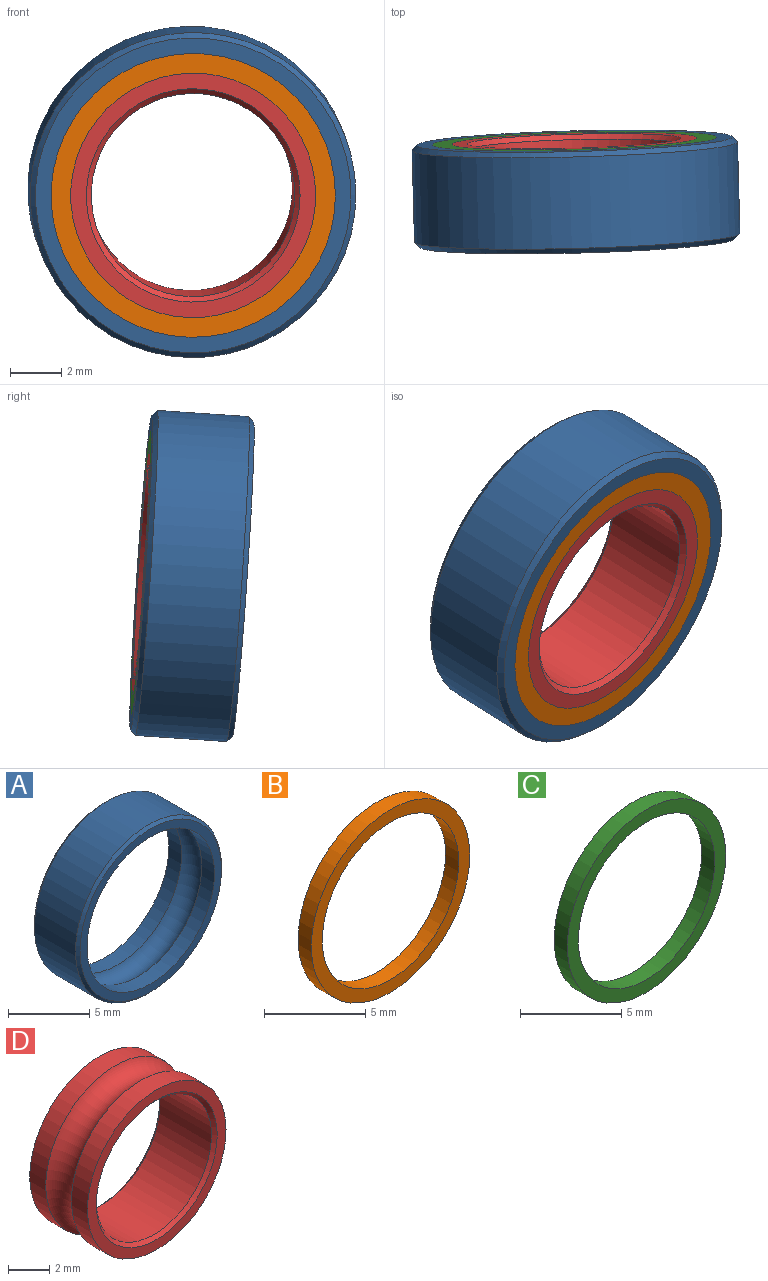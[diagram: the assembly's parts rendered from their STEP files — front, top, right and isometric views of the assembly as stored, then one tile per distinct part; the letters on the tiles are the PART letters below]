
ASSEMBLY  parts=4 mates=6
PART A: 8 faces, bbox 13.3x4x13.3 mm
  f0: cone r=6.35mm half-angle=45deg, axis (0,1,0), area 11mm2, adj f1,f7
  f1: cylinder r=6.35mm len=12.7mm, axis (0,-1,0), area 142.5mm2, adj f0,f2
  f2: cone r=6.15mm half-angle=45deg, axis (0,-1,0), area 11mm2, adj f1,f3
  f3: plane 12.3x12.3mm, normal (0,1,0), area 22.4mm2, adj f2,f4
  f4: cylinder r=5.54mm len=11.09mm, axis (0,-1,0), area 38.4mm2, adj f3,f5
  f5: torus R=5.16mm, axis (0,-1,0), area 83mm2, adj f4,f6
  f6: cylinder r=5.54mm len=11.09mm, axis (0,-1,0), area 38.4mm2, adj f5,f7
  f7: plane 12.3x12.3mm, normal (0,-1,0), area 22.4mm2, adj f0,f6
PART B: 4 faces, bbox 11.1x0.9x11.1 mm
  f0: plane 11.09x11.09mm, normal (0,-1,0), area 24.9mm2, adj f1,f3
  f1: cylinder r=4.78mm len=9.55mm, axis (0,-1,0), area 27.7mm2, adj f0,f2
  f2: plane 11.09x11.09mm, normal (0,1,0), area 24.9mm2, adj f1,f3
  f3: cylinder r=5.54mm len=11.09mm, axis (0,-1,0), area 32.2mm2, adj f0,f2
PART C: 4 faces, bbox 11.1x0.9x11.1 mm
  f0: plane 11.09x11.09mm, normal (0,1,0), area 24.9mm2, adj f1,f3
  f1: cylinder r=4.78mm len=9.55mm, axis (0,-1,0), area 27.7mm2, adj f0,f2
  f2: plane 11.09x11.09mm, normal (0,-1,0), area 24.9mm2, adj f1,f3
  f3: cylinder r=5.54mm len=11.09mm, axis (0,-1,0), area 32.2mm2, adj f0,f2
PART D: 8 faces, bbox 11.2x4x11.2 mm
  f0: plane 9.55x9.55mm, normal (0,-1,0), area 17.1mm2, adj f1,f7
  f1: cylinder r=4.78mm len=9.55mm, axis (0,-1,0), area 33.1mm2, adj f0,f2
  f2: torus R=5.16mm, axis (0,-1,0), area 61.7mm2, adj f1,f3
  f3: cylinder r=4.78mm len=9.55mm, axis (0,-1,0), area 33.1mm2, adj f2,f4
  f4: plane 9.55x9.55mm, normal (0,1,0), area 17.1mm2, adj f3,f5
  f5: cone r=3.97mm half-angle=45deg, axis (0,1,0), area 7.2mm2, adj f4,f6
  f6: cylinder r=3.97mm len=7.94mm, axis (0,-1,0), area 89.1mm2, adj f5,f7
  f7: cone r=4.17mm half-angle=45deg, axis (0,-1,0), area 7.2mm2, adj f0,f6
PLACE A rot(axis=(0.93,-0.03,0.37),4.1deg) t=(1.2,-2.45,-2.15)mm
PLACE B rot(axis=(-1,-0.01,0),176.1deg) t=(1.28,-5.39,-2.34)mm
PLACE C rot(axis=(0.93,-0.03,0.37),4.1deg) t=(1.2,-2.36,-2.14)mm
PLACE D rot(axis=(0.93,-0.03,0.37),4.1deg) t=(1.2,-2.45,-2.15)mm
MATE planar B.f1 <-> D.f1  axis (0.03,-1,-0.07) through (1.25,-4.43,-2.28)mm
MATE planar A.f0 <-> D.f1  axis (0.03,-1,-0.07) through (1.25,-4.43,-2.28)mm
MATE planar C.f1 <-> A.f0  axis (-0.03,1,0.07) through (1.14,-0.48,-2.01)mm
MATE cylindrical B.f1 <-> A.f0  axis (0.03,-1,-0.07) through (1.25,-4.43,-2.28)mm
MATE cylindrical C.f1 <-> A.f0  axis (-0.03,1,0.07) through (1.14,-0.48,-2.01)mm
MATE cylindrical D.f1 <-> A.f0  axis (-0.03,1,0.07) through (1.14,-0.48,-2.01)mm
